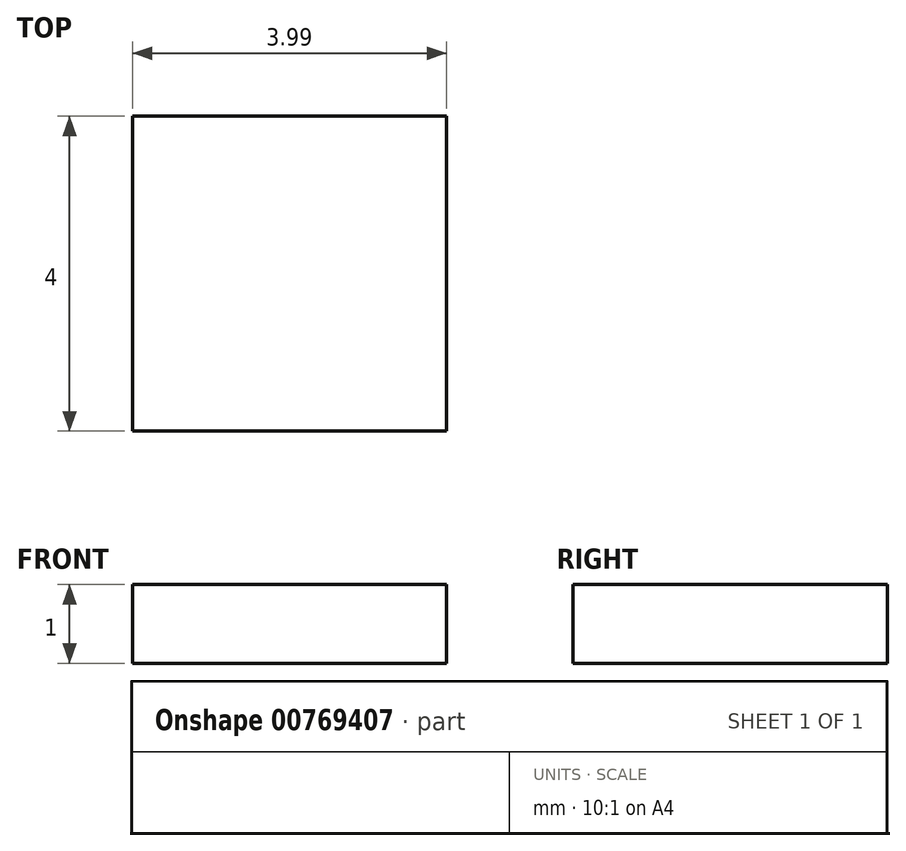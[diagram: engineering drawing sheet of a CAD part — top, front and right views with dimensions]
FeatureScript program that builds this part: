
annotation { "Feature Type Name" : "Feature", "Feature Type Description" : "" }
export const myFeature = defineFeature(function(context is Context, id is Id, definition is map)
    precondition{}
    {
        {
            var Q0;
            Q0=qCreatedBy(makeId("Top.planeOp"),FACE);
            var sketch = newSketch(context, id + "F0", { "sketchPlane" : qUnion([Q0])});
            skLineSegment(sketch, "E0.bottom", {"start": v(-7.44, -13.26) * mm, "end": v(-3.45, -13.26) * mm});
            skLineSegment(sketch, "E0.top", {"start": v(-7.44, -9.26) * mm, "end": v(-3.45, -9.26) * mm});
            skLineSegment(sketch, "E0.left", {"start": v(-7.44, -13.26) * mm, "end": v(-7.44, -9.26) * mm});
            skLineSegment(sketch, "E0.right", {"start": v(-3.45, -13.26) * mm, "end": v(-3.45, -9.26) * mm});
            skSolve(sketch);
        }
        {
            var Q0;
            Q0=makeQuery(id+"F0.imprint","IMPRINT",FACE,{"disambiguationData":[TD([[makeQuery(id+"F0.imprint","IMPRINT",EDGE,{"derivedFrom":sQuery(id+"F0.wireOp",EDGE,"E0.bottom")}),1.0]])]});
            var Q1;
            Q1 = qSketchRegion(id + "F0", true);
            extrude(context, id + "F1", {"entities" : qUnion([Q0, Q1]), "depth" : 1 * mm, "offsetDistance" : 25 * mm});
        }
    });
